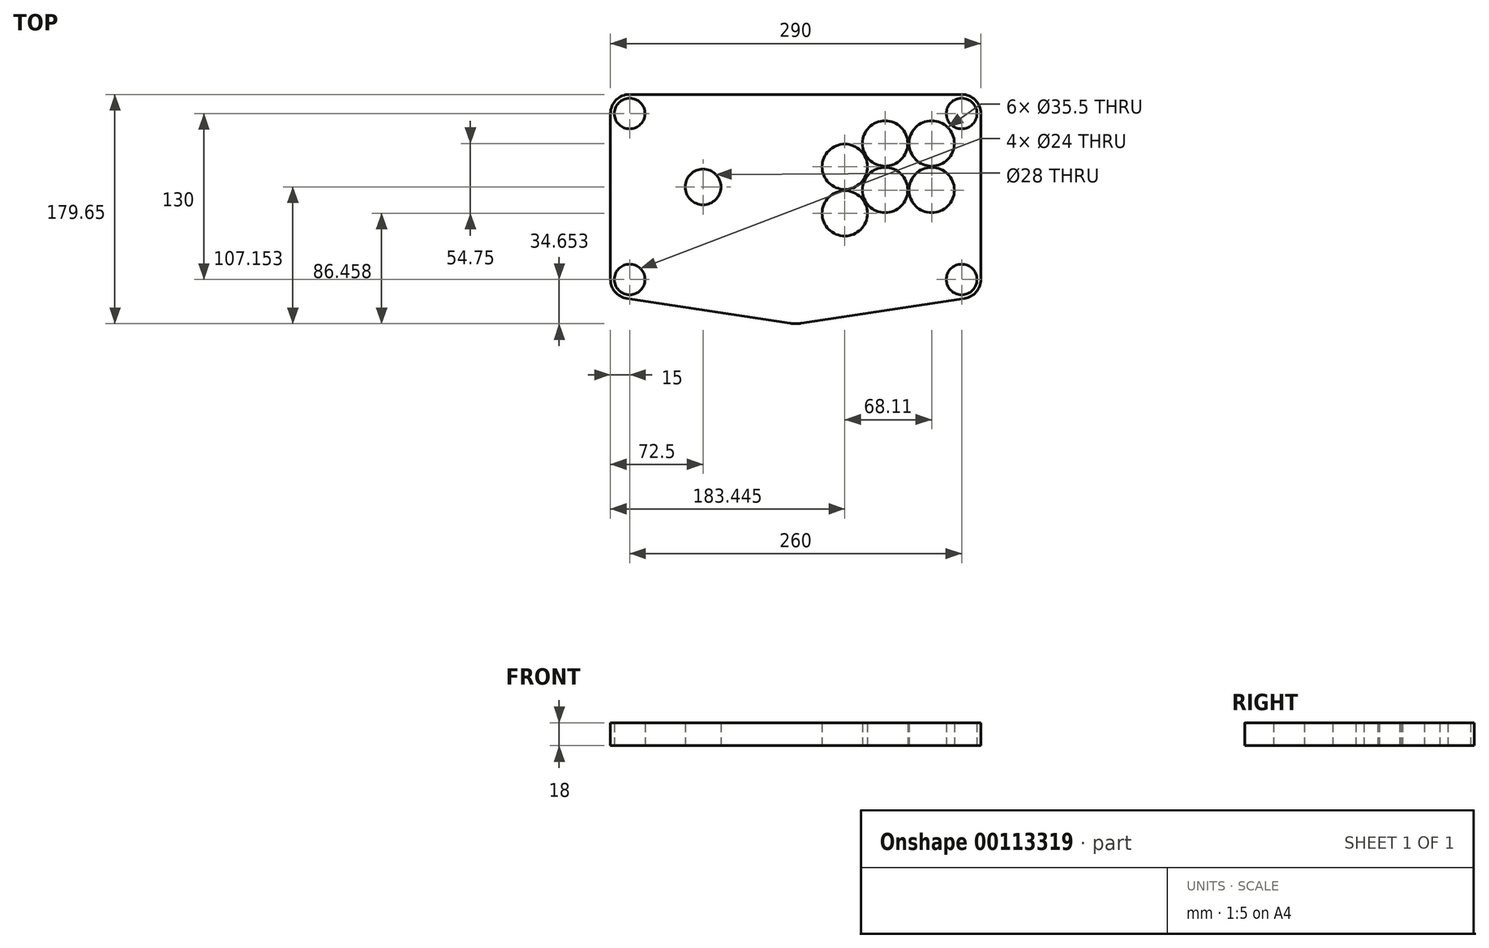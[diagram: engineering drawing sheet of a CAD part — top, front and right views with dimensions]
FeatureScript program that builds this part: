
annotation { "Feature Type Name" : "Feature", "Feature Type Description" : "" }
export const myFeature = defineFeature(function(context is Context, id is Id, definition is map)
    precondition{}
    {
        {
            var Q0;
            Q0=qCreatedBy(makeId("Top.planeOp"),FACE);
            var sketch = newSketch(context, id + "F0", { "sketchPlane" : qUnion([Q0])});
            skLineSegment(sketch, "E0.bottom", {"start": v(130, 78.94) * mm, "end": v(-130, 78.94) * mm});
            skLineSegment(sketch, "E0.left", {"start": v(145, 63.94) * mm, "end": v(145, -66.06) * mm});
            skLineSegment(sketch, "E0.right", {"start": v(-145, 63.94) * mm, "end": v(-145, -66.06) * mm});
            skPoint(sketch, "E0.middle", {"position": v(0, 0) * mm});
            skPoint(sketch, "E1.endSnap0", {"position": v(0, 78.94) * mm});
            skLineSegment(sketch, "E2", {"start": v(4.52, -100.37) * mm, "end": v(132.26, -80.89) * mm});
            skLineSegment(sketch, "E3", {"start": v(-4.52, -100.37) * mm, "end": v(-132.26, -80.89) * mm});
            skPoint(sketch, "E4.visualSharp", {"position": v(-145, -78.94) * mm});
            skArc(sketch, "E4.filletArc", {"start": v(-145, -66.06) * mm, "mid": v(-141.38, -75.83) * mm, "end": v(-132.26, -80.89) * mm});
            skPoint(sketch, "E5.visualSharp", {"position": v(-145, 78.94) * mm});
            skArc(sketch, "E5.filletArc", {"start": v(-130, 78.94) * mm, "mid": v(-140.6, 74.55) * mm, "end": v(-145, 63.94) * mm});
            skPoint(sketch, "E6.visualSharp", {"position": v(145, 78.94) * mm});
            skArc(sketch, "E6.filletArc", {"start": v(145, 63.94) * mm, "mid": v(140.6, 74.55) * mm, "end": v(130, 78.94) * mm});
            skPoint(sketch, "E7.visualSharp", {"position": v(145, -78.94) * mm});
            skArc(sketch, "E7.filletArc", {"start": v(132.26, -80.89) * mm, "mid": v(141.38, -75.83) * mm, "end": v(145, -66.06) * mm});
            skPoint(sketch, "E8.visualSharp", {"position": v(0, -101.06) * mm});
            skArc(sketch, "E8.filletArc", {"start": v(-4.52, -100.37) * mm, "mid": v(0, -100.71) * mm, "end": v(4.52, -100.37) * mm});
            skLineSegment(sketch, "E9", {"start": v(0, 78.94) * mm, "end": v(0, -101.06) * mm, "construction": true});
            skCircle(sketch, "E10", {"center": v(130, 63.94) * mm, "radius": 12 * mm});
            skCircle(sketch, "E11", {"center": v(130, -66.06) * mm, "radius": 12 * mm});
            skCircle(sketch, "E12", {"center": v(-130, 63.94) * mm, "radius": 12 * mm});
            skCircle(sketch, "E13", {"center": v(-130, -66.06) * mm, "radius": 12 * mm});
            skCircle(sketch, "E14", {"center": v(106.55, 40.5) * mm, "radius": 17.75 * mm});
            skCircle(sketch, "E15", {"center": v(106.55, 4) * mm, "radius": 17.75 * mm});
            skLineSegment(sketch, "E16", {"start": v(106.55, 4) * mm, "end": v(106.55, 40.5) * mm, "construction": true});
            skLineSegment(sketch, "E17", {"start": v(106.55, 4) * mm, "end": v(70.05, 4) * mm, "construction": true});
            skLineSegment(sketch, "E18", {"start": v(70.05, 4) * mm, "end": v(70.05, 40.5) * mm, "construction": true});
            skLineSegment(sketch, "E19", {"start": v(70.05, 40.5) * mm, "end": v(106.55, 40.5) * mm, "construction": true});
            skCircle(sketch, "E20", {"center": v(70.05, 40.5) * mm, "radius": 17.75 * mm});
            skCircle(sketch, "E21", {"center": v(70.05, 4) * mm, "radius": 17.75 * mm});
            skCircle(sketch, "E22", {"center": v(38.45, 22.25) * mm, "radius": 17.75 * mm});
            skCircle(sketch, "E23", {"center": v(38.45, -14.25) * mm, "radius": 17.75 * mm});
            skCircle(sketch, "E24", {"center": v(-72.5, 6.44) * mm, "radius": 14 * mm});
            skLineSegment(sketch, "E25", {"start": v(-72.5, 6.44) * mm, "end": v(-145, 6.44) * mm, "construction": true});
            skLineSegment(sketch, "E26", {"start": v(-72.5, 6.44) * mm, "end": v(-72.5, 78.94) * mm, "construction": true});
            skLineSegment(sketch, "E27", {"start": v(106.55, 40.5) * mm, "end": v(145, 40.5) * mm, "construction": true});
            skLineSegment(sketch, "E28", {"start": v(106.55, 40.5) * mm, "end": v(106.55, 78.94) * mm, "construction": true});
            skSolve(sketch);
        }
        {
            var Q0;
            Q0=makeQuery(id+"F0.imprint","IMPRINT",FACE,{"disambiguationData":[TD([[makeQuery(id+"F0.imprint","IMPRINT",EDGE,{"derivedFrom":sQuery(id+"F0.wireOp",EDGE,"E0.bottom")}),1.0]])]});
            extrude(context, id + "F1", {"entities" : qUnion([Q0]), "depth" : 18 * mm});
        }
    });
